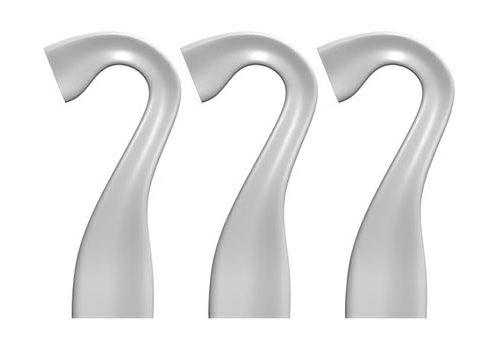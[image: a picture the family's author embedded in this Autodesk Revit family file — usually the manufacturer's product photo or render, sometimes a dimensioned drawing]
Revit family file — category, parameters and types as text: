
# Revit family: CITY ALPHABET litera „M”
name_source: partatom
category: Meble
revit_build: Autodesk Revit 2018 (Build: 20190510_1515(x64)
units: mm (PartAtom-declared; Revit-internal decimal feet)

## family parameters
Numer OmniClass = 23.40.10.11.14
Obiekt nadrzędny = Powierzchnia
Punkt obliczania pomieszczeń = Nie
Tnij formami wycięć po wczytaniu = Nie
Tytuł OmniClass = Exterior Seating
Współdzielony = Nie

## types (1)
- CITY ALPHABET litera „M”
    Domyślna rzędna = 1219 mm
    Długość = 3350 mm  [stored 10.9908 ft]
    IfcExportAs = IfcFurnishingElement
    Komentarze do typu = Ławka
    Materiał - informacja = Szeroki wybór kolorów wg palety RAL. Istnieje również możliwość specjalnego wykonania
kolorystycznego na indywidualne zapytanie klienta.
    Model = CITY ALPHABET litera „M”
    Obraz typu = M.jpg
    Producent = Astrini Design
    Szerokość = 2350 mm
    Temepratura użytkowania = -40°C do 80°C, ( -40°F do 176°F )
    URL = http://astrini-design.pl
    Waga (szacunkowo) = 103.50 kg
    Waga po wypełnieniu (szacunkowo) = 254.00 kg
    Wysokość = 420 mm  [stored 1.37795 ft]

note: [stored X ft] marks values corroborated as IEEE doubles in the binary element streams (Revit-internal decimal feet)
